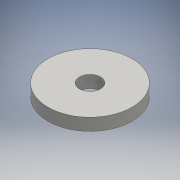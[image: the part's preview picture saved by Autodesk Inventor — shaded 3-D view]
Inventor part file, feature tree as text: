
AUTODESK INVENTOR PART (.ipt)
format: ipt  version: 2016 (Build 200138000, 138)  size: 92,160 bytes
history: native  units: mm
features: other x1, extrude x1, sketch x1
ambient origin geometry x8: Origin, YZ Plane, XZ Plane, XY Plane, X Axis, Y Axis, Z Axis, Center Point
bodies: Body1 (feature_tree)
feature tree (3):
  other  "ソリッド1"
  extrude  "押し出し1"  Depth=12.0mm
  sketch  "スケッチ1"
